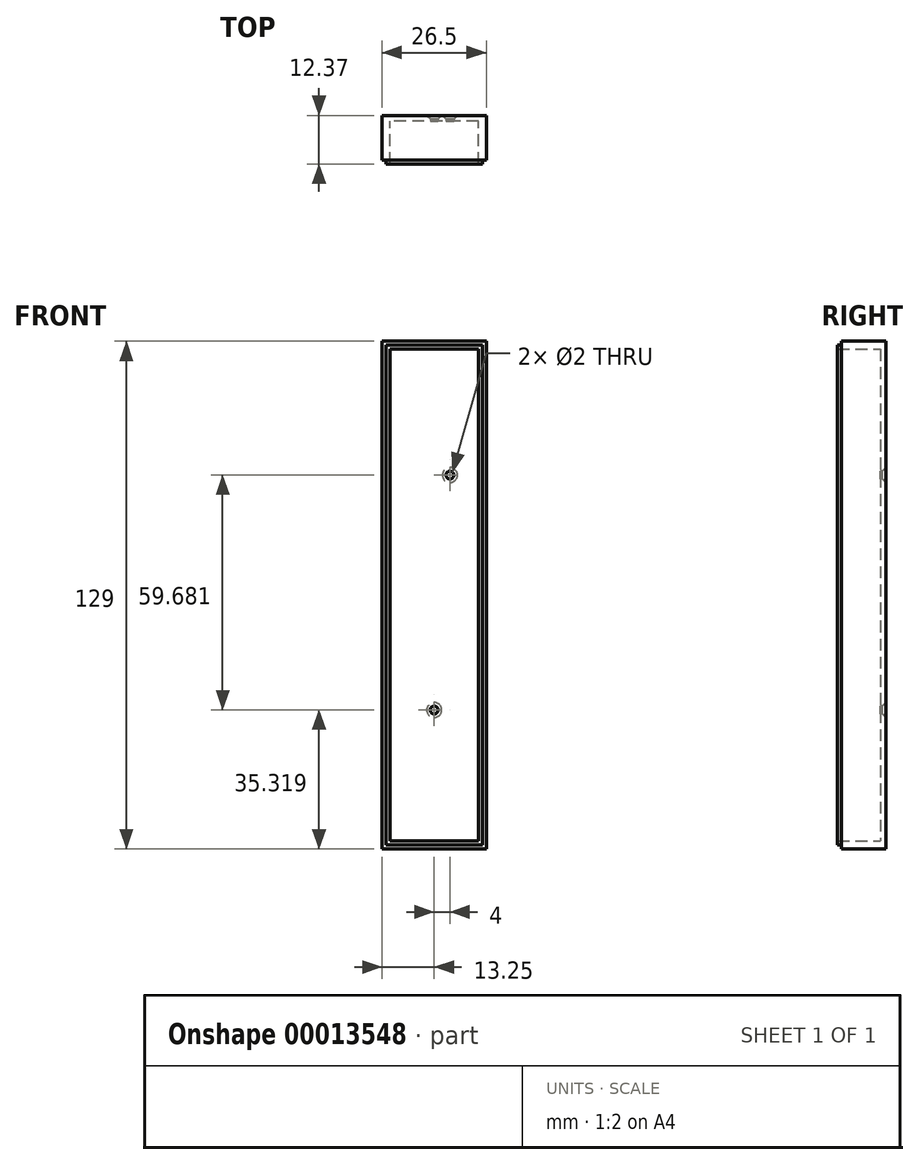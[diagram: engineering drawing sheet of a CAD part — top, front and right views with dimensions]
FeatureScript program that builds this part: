
annotation { "Feature Type Name" : "Feature", "Feature Type Description" : "" }
export const myFeature = defineFeature(function(context is Context, id is Id, definition is map)
    precondition{}
    {
        {
            var Q0;
            Q0=qCreatedBy(makeId("Front.planeOp"),FACE);
            var sketch = newSketch(context, id + "F0", { "sketchPlane" : qUnion([Q0])});
            skLineSegment(sketch, "E0.rect.bottom", {"start": v(13.25, 64.5) * mm, "end": v(-13.25, 64.5) * mm});
            skLineSegment(sketch, "E0.rect.top", {"start": v(13.25, -64.5) * mm, "end": v(-13.25, -64.5) * mm});
            skLineSegment(sketch, "E0.rect.left", {"start": v(13.25, 64.5) * mm, "end": v(13.25, -64.5) * mm});
            skLineSegment(sketch, "E0.rect.right", {"start": v(-13.25, 64.5) * mm, "end": v(-13.25, -64.5) * mm});
            skPoint(sketch, "E0.rect.middle", {"position": v(0, 0) * mm});
            skSolve(sketch);
        }
        {
            var Q0;
            Q0 = qSketchRegion(id + "F0", true);
            extrude(context, id + "F1", {"entities" : qUnion([Q0]), "depth" : 11.37 * mm});
        }
        {
            var Q0;
            Q0=makeQuery(id+"F1.opExtrude","CAP_FACE",FACE,{"disambiguationData":[OSD([sQuery(id+"F0.wireOp",EDGE,"E0.rect.bottom"),sQuery(id+"F0.wireOp",EDGE,"E0.rect.top"),sQuery(id+"F0.wireOp",EDGE,"E0.rect.left"),sQuery(id+"F0.wireOp",EDGE,"E0.rect.right")])],"isStart":false});
            shell(context, id + "F2", {"entities" : qUnion([Q0]), "thickness" : 2 * mm});
        }
        {
            var Q0;
            Q0=makeQuery(id+"F2.opShell","OFFSET_FACE",FACE,{"disambiguationData":[OSD([sQuery(id+"F0.wireOp",EDGE,"E0.rect.bottom"),sQuery(id+"F0.wireOp",EDGE,"E0.rect.top"),sQuery(id+"F0.wireOp",EDGE,"E0.rect.left"),sQuery(id+"F0.wireOp",EDGE,"E0.rect.right")])]});
            var sketch = newSketch(context, id + "F3", { "sketchPlane" : qUnion([Q0])});
            skLineSegment(sketch, "E1.rect.bottom", {"start": v(-11.25, 62.5) * mm, "end": v(11.25, 62.5) * mm});
            skLineSegment(sketch, "E1.rect.top", {"start": v(-11.25, -62.5) * mm, "end": v(11.25, -62.5) * mm});
            skLineSegment(sketch, "E1.rect.left", {"start": v(-11.25, 62.5) * mm, "end": v(-11.25, -62.5) * mm});
            skLineSegment(sketch, "E1.rect.right", {"start": v(11.25, 62.5) * mm, "end": v(11.25, -62.5) * mm});
            skPoint(sketch, "E1.rect.middle", {"position": v(0, 0) * mm});
            skSolve(sketch);
        }
        {
            var Q0;
            Q0 = qSketchRegion(id + "F3", true);
            extrude(context, id + "F4", {"entities" : qUnion([Q0]), "operationType" : NewBodyOperationType.REMOVE, "oppositeDirection" : true, "depth" : .5 * mm});
        }
        {
            var Q0;
            Q0=makeQuery(id+"F1.opExtrude","CAP_FACE",FACE,{"disambiguationData":[OSD([sQuery(id+"F0.wireOp",EDGE,"E0.rect.bottom"),sQuery(id+"F0.wireOp",EDGE,"E0.rect.top"),sQuery(id+"F0.wireOp",EDGE,"E0.rect.left"),sQuery(id+"F0.wireOp",EDGE,"E0.rect.right")])],"isStart":false});
            var sketch = newSketch(context, id + "F5", { "sketchPlane" : qUnion([Q0])});
            skLineSegment(sketch, "E2.rect.bottom", {"start": v(11.25, -62.5) * mm, "end": v(-11.25, -62.5) * mm});
            skLineSegment(sketch, "E2.rect.top", {"start": v(11.25, 62.5) * mm, "end": v(-11.25, 62.5) * mm});
            skLineSegment(sketch, "E2.rect.left", {"start": v(11.25, -62.5) * mm, "end": v(11.25, 62.5) * mm});
            skLineSegment(sketch, "E2.rect.right", {"start": v(-11.25, -62.5) * mm, "end": v(-11.25, 62.5) * mm});
            skPoint(sketch, "E2.rect.middle", {"position": v(0, 0) * mm});
            skLineSegment(sketch, "E3.rect.bottom", {"start": v(12.25, -63.5) * mm, "end": v(-12.25, -63.5) * mm});
            skLineSegment(sketch, "E3.rect.top", {"start": v(12.25, 63.5) * mm, "end": v(-12.25, 63.5) * mm});
            skLineSegment(sketch, "E3.rect.left", {"start": v(12.25, -63.5) * mm, "end": v(12.25, 63.5) * mm});
            skLineSegment(sketch, "E3.rect.right", {"start": v(-12.25, -63.5) * mm, "end": v(-12.25, 63.5) * mm});
            skSolve(sketch);
        }
        {
            var Q0;
            Q0 = qSketchRegion(id + "F5", true);
            extrude(context, id + "F6", {"entities" : qUnion([Q0]), "operationType" : NewBodyOperationType.ADD, "depth" : 1 * mm});
        }
        {
            var Q0;
            {var subQ0=sQuery(id+"F0.wireOp",EDGE,"E0.rect.bottom");var subQ1=sQuery(id+"F0.wireOp",EDGE,"E0.rect.top");var subQ2=sQuery(id+"F0.wireOp",EDGE,"E0.rect.left");var subQ3=sQuery(id+"F0.wireOp",EDGE,"E0.rect.right");Q0=makeQuery(id+"FY79sKiWcl9OTak_1.boolean.opBoolean","SPLIT",FACE,{"disambiguationData":[TD([makeQuery(id+"F1.opExtrude","SWEPT_FACE",FACE,{"disambiguationData":[OSD([subQ0])]})])],"derivedFrom":makeQuery(id+"F1.opExtrude","CAP_FACE",FACE,{"disambiguationData":[OSD([subQ0,subQ1,subQ2,subQ3])],"isStart":true})});}
            var sketch = newSketch(context, id + "F7", { "sketchPlane" : qUnion([Q0])});
            skLineSegment(sketch, "E4", {"start": v(11.25, 62.5) * mm, "end": v(-11.25, 62.5) * mm, "construction": true});
            skPoint(sketch, "E5", {"position": v(-4, 30.5) * mm});
            skPoint(sketch, "E6.0.MirrorP", {"position": v(0, -29.18) * mm});
            skLineSegment(sketch, "E7", {"start": v(0, 62.5) * mm, "end": v(0, -64.5) * mm, "construction": true});
            skSolve(sketch);
        }
        {
            var Q0;
            Q0=sQuery(id+"F7.wireOp",VERTEX,"E5");
            var Q1;
            Q1=sQuery(id+"F7.wireOp",VERTEX,"E6.0.MirrorP");
            var Q2;
            Q2=makeQuery(id+"F1.opExtrude","SWEPT_BODY",BODY,{"disambiguationData":[OSD([sQuery(id+"F0.wireOp",EDGE,"E0.rect.bottom"),sQuery(id+"F0.wireOp",EDGE,"E0.rect.top"),sQuery(id+"F0.wireOp",EDGE,"E0.rect.left"),sQuery(id+"F0.wireOp",EDGE,"E0.rect.right")])]});
            hole(context, id + "F8", {"style" : HoleStyle.C_SINK, "holeDiameter" : 2 * mm, "cSinkDiameter" : 3.8 * mm, "endStyle" : HoleEndStyle.THROUGH, "locations" : qUnion([Q0, Q1]), "scope" : qUnion([Q2]), "cSinkAngle" : 90 * degree});
        }
    });
